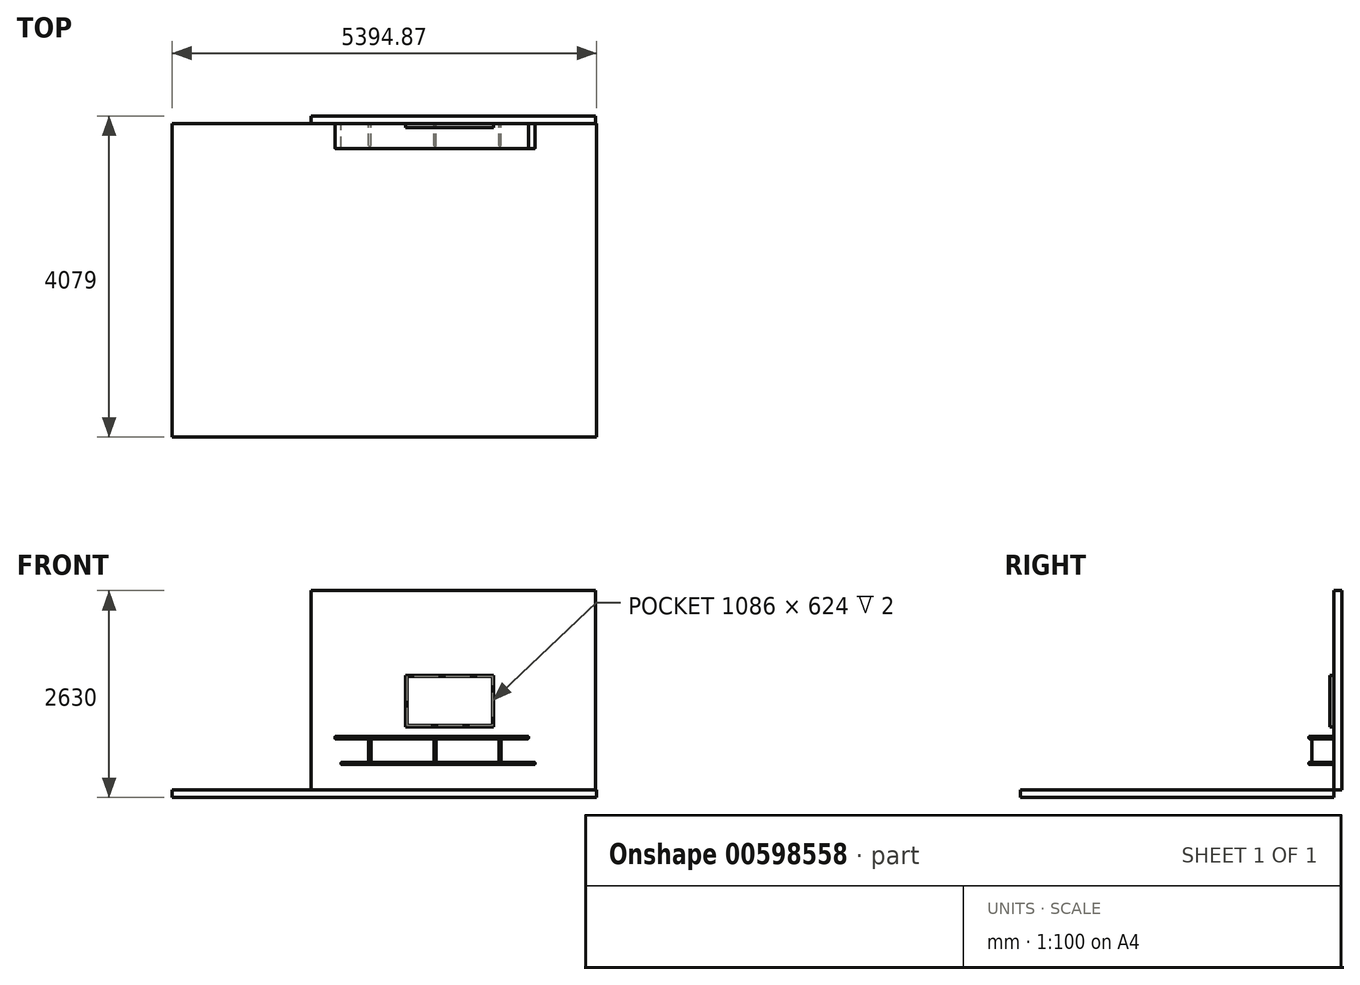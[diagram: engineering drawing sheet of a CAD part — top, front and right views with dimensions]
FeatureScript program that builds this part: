
annotation { "Feature Type Name" : "Feature", "Feature Type Description" : "" }
export const myFeature = defineFeature(function(context is Context, id is Id, definition is map)
    precondition{}
    {
        {
            var Q0;
            Q0=qCreatedBy(makeId("Front.planeOp"),FACE);
            var sketch = newSketch(context, id + "F0", { "sketchPlane" : qUnion([Q0])});
            skLineSegment(sketch, "E0.bottom", {"start": v(-1805, 0) * mm, "end": v(1805, 0) * mm});
            skLineSegment(sketch, "E0.top", {"start": v(-1805, 2530) * mm, "end": v(1805, 2530) * mm});
            skLineSegment(sketch, "E0.left", {"start": v(-1805, 0) * mm, "end": v(-1805, 2530) * mm});
            skLineSegment(sketch, "E0.right", {"start": v(1805, 0) * mm, "end": v(1805, 2530) * mm});
            skPoint(sketch, "E1", {"position": v(0, 0) * mm});
            skSolve(sketch);
        }
        {
            var Q0;
            Q0=makeQuery(id+"F0.imprint","IMPRINT",FACE,{"disambiguationData":[TD([[makeQuery(id+"F0.imprint","IMPRINT",EDGE,{"derivedFrom":sQuery(id+"F0.wireOp",EDGE,"E0.bottom")}),1.0]])]});
            extrude(context, id + "F1", {"entities" : qUnion([Q0]), "oppositeDirection" : true, "depth" : 100 * mm, "offsetDistance" : 25 * mm});
        }
        {
            var Q0;
            Q0=qCreatedBy(makeId("Top.planeOp"),FACE);
            var sketch = newSketch(context, id + "F2", { "sketchPlane" : qUnion([Q0])});
            skLineSegment(sketch, "E2.bottom", {"start": v(1820.18, 0) * mm, "end": v(-3574.69, 0) * mm});
            skLineSegment(sketch, "E2.top", {"start": v(1820.18, -3979) * mm, "end": v(-3574.69, -3979) * mm});
            skLineSegment(sketch, "E2.left", {"start": v(1820.18, 0) * mm, "end": v(1820.18, -3979) * mm});
            skLineSegment(sketch, "E2.right", {"start": v(-3574.69, 0) * mm, "end": v(-3574.69, -3979) * mm});
            skSolve(sketch);
        }
        {
            var Q0;
            Q0 = qSketchRegion(id + "F2", true);
            extrude(context, id + "F3", {"entities" : qUnion([Q0]), "operationType" : NewBodyOperationType.ADD, "oppositeDirection" : true, "depth" : 100 * mm, "offsetDistance" : 25 * mm});
        }
        {
            var Q0;
            Q0=makeQuery(id+"F1.opExtrude","CAP_FACE",FACE,{"disambiguationData":[OSD([sQuery(id+"F0.wireOp",EDGE,"E0.bottom"),sQuery(id+"F0.wireOp",EDGE,"E0.top"),sQuery(id+"F0.wireOp",EDGE,"E0.left"),sQuery(id+"F0.wireOp",EDGE,"E0.right")])],"isStart":true});
            var sketch = newSketch(context, id + "F4", { "sketchPlane" : qUnion([Q0])});
            skLineSegment(sketch, "E3.bottom", {"start": v(511, 800) * mm, "end": v(-605, 800) * mm});
            skLineSegment(sketch, "E3.top", {"start": v(511, 1454) * mm, "end": v(-605, 1454) * mm});
            skLineSegment(sketch, "E3.left", {"start": v(511, 800) * mm, "end": v(511, 1454) * mm});
            skLineSegment(sketch, "E3.right", {"start": v(-605, 800) * mm, "end": v(-605, 1454) * mm});
            skPoint(sketch, "E3.middle", {"position": v(-47, 1127) * mm});
            skSolve(sketch);
        }
        {
            var Q0;
            Q0 = qSketchRegion(id + "F4", true);
            extrude(context, id + "F5", {"entities" : qUnion([Q0]), "depth" : 50 * mm, "offsetDistance" : 25 * mm});
        }
        {
            var Q0;
            Q0=makeQuery(id+"F5.opExtrude","CAP_FACE",FACE,{"disambiguationData":[OSD([sQuery(id+"F4.wireOp",EDGE,"E3.bottom"),sQuery(id+"F4.wireOp",EDGE,"E3.top"),sQuery(id+"F4.wireOp",EDGE,"E3.left"),sQuery(id+"F4.wireOp",EDGE,"E3.right")])],"isStart":false});
            var sketch = newSketch(context, id + "F6", { "sketchPlane" : qUnion([Q0])});
            skLineSegment(sketch, "E4.bottom", {"start": v(-590, 1439) * mm, "end": v(496, 1439) * mm});
            skLineSegment(sketch, "E4.top", {"start": v(-590, 815) * mm, "end": v(496, 815) * mm});
            skLineSegment(sketch, "E4.left", {"start": v(-590, 1439) * mm, "end": v(-590, 815) * mm});
            skLineSegment(sketch, "E4.right", {"start": v(496, 1439) * mm, "end": v(496, 815) * mm});
            skSolve(sketch);
        }
        {
            var Q0;
            Q0 = qSketchRegion(id + "F6", true);
            extrude(context, id + "F7", {"entities" : qUnion([Q0]), "operationType" : NewBodyOperationType.REMOVE, "oppositeDirection" : true, "depth" : 2 * mm, "offsetDistance" : 25 * mm});
        }
        {
            var Q0;
            Q0=makeQuery(id+"F1.opExtrude","CAP_FACE",FACE,{"disambiguationData":[OSD([sQuery(id+"F0.wireOp",EDGE,"E0.bottom"),sQuery(id+"F0.wireOp",EDGE,"E0.top"),sQuery(id+"F0.wireOp",EDGE,"E0.left"),sQuery(id+"F0.wireOp",EDGE,"E0.right")])],"isStart":true});
            var sketch = newSketch(context, id + "F8", { "sketchPlane" : qUnion([Q0])});
            skLineSegment(sketch, "E5.bottom", {"start": v(-1505, 676) * mm, "end": v(955, 676) * mm});
            skLineSegment(sketch, "E5.top", {"start": v(-1505, 648) * mm, "end": v(955, 648) * mm});
            skLineSegment(sketch, "E5.left", {"start": v(-1505, 676) * mm, "end": v(-1505, 648) * mm});
            skLineSegment(sketch, "E5.right", {"start": v(955, 676) * mm, "end": v(955, 648) * mm});
            skLineSegment(sketch, "E6.bottom", {"start": v(-1424.33, 348) * mm, "end": v(1035.67, 348) * mm});
            skLineSegment(sketch, "E6.top", {"start": v(-1424.33, 320) * mm, "end": v(1035.67, 320) * mm});
            skLineSegment(sketch, "E6.left", {"start": v(-1424.33, 348) * mm, "end": v(-1424.33, 320) * mm});
            skLineSegment(sketch, "E6.right", {"start": v(1035.67, 348) * mm, "end": v(1035.67, 320) * mm});
            skSolve(sketch);
        }
        {
            var Q0;
            Q0 = qSketchRegion(id + "F8", true);
            extrude(context, id + "F9", {"entities" : qUnion([Q0]), "depth" : 315 * mm, "offsetDistance" : 25 * mm});
        }
        {
            var Q0;
            Q0=makeQuery(id+"F1.opExtrude","CAP_FACE",FACE,{"disambiguationData":[OSD([sQuery(id+"F0.wireOp",EDGE,"E0.bottom"),sQuery(id+"F0.wireOp",EDGE,"E0.top"),sQuery(id+"F0.wireOp",EDGE,"E0.left"),sQuery(id+"F0.wireOp",EDGE,"E0.right")])],"isStart":true});
            var sketch = newSketch(context, id + "F10", { "sketchPlane" : qUnion([Q0])});
            skLineSegment(sketch, "E7.bottom", {"start": v(-1074.33, 348) * mm, "end": v(-1046.33, 348) * mm});
            skLineSegment(sketch, "E7.top", {"start": v(-1074.33, 648) * mm, "end": v(-1046.33, 648) * mm});
            skLineSegment(sketch, "E7.left", {"start": v(-1074.33, 348) * mm, "end": v(-1074.33, 648) * mm});
            skLineSegment(sketch, "E7.right", {"start": v(-1046.33, 348) * mm, "end": v(-1046.33, 648) * mm});
            skLineSegment(sketch, "E8.bottom", {"start": v(577, 348) * mm, "end": v(605, 348) * mm});
            skLineSegment(sketch, "E8.top", {"start": v(577, 648) * mm, "end": v(605, 648) * mm});
            skLineSegment(sketch, "E8.left", {"start": v(577, 348) * mm, "end": v(577, 648) * mm});
            skLineSegment(sketch, "E8.right", {"start": v(605, 348) * mm, "end": v(605, 648) * mm});
            skLineSegment(sketch, "E9.bottom", {"start": v(-247.43, 348) * mm, "end": v(-219.43, 348) * mm});
            skLineSegment(sketch, "E9.top", {"start": v(-247.43, 648) * mm, "end": v(-219.43, 648) * mm});
            skLineSegment(sketch, "E9.left", {"start": v(-247.43, 348) * mm, "end": v(-247.43, 648) * mm});
            skLineSegment(sketch, "E9.right", {"start": v(-219.43, 348) * mm, "end": v(-219.43, 648) * mm});
            skSolve(sketch);
        }
        {
            var Q0;
            Q0 = qSketchRegion(id + "F10", true);
            extrude(context, id + "F11", {"entities" : qUnion([Q0]), "depth" : 280 * mm, "offsetDistance" : 25 * mm});
        }
        {
            var Q0;
            Q0=makeQuery(id+"F9.opExtrude","CAP_EDGE",EDGE,{"disambiguationData":[OSD([sQuery(id+"F8.wireOp",EDGE,"E5.left")])],"isStart":false});
            var Q1;
            Q1=makeQuery(id+"F9.opExtrude","SWEPT_EDGE",EDGE,{"disambiguationData":[OSD([sQuery(id+"F8.wireOp",EDGE,"E5.bottom"),sQuery(id+"F8.wireOp",EDGE,"E5.left")])]});
            var Q2;
            Q2=makeQuery(id+"F9.opExtrude","SWEPT_EDGE",EDGE,{"disambiguationData":[OSD([sQuery(id+"F8.wireOp",EDGE,"E5.top"),sQuery(id+"F8.wireOp",EDGE,"E5.left")])]});
            var Q3;
            Q3=makeQuery(id+"F9.opExtrude","CAP_EDGE",EDGE,{"disambiguationData":[OSD([sQuery(id+"F8.wireOp",EDGE,"E5.top")])],"isStart":false});
            var Q4;
            Q4=makeQuery(id+"F9.opExtrude","CAP_EDGE",EDGE,{"disambiguationData":[OSD([sQuery(id+"F8.wireOp",EDGE,"E5.bottom")])],"isStart":false});
            var Q5;
            Q5=makeQuery(id+"F9.opExtrude","SWEPT_EDGE",EDGE,{"disambiguationData":[OSD([sQuery(id+"F8.wireOp",EDGE,"E6.bottom"),sQuery(id+"F8.wireOp",EDGE,"E6.left")])]});
            var Q6;
            Q6=makeQuery(id+"F9.opExtrude","SWEPT_EDGE",EDGE,{"disambiguationData":[OSD([sQuery(id+"F8.wireOp",EDGE,"E6.top"),sQuery(id+"F8.wireOp",EDGE,"E6.left")])]});
            var Q7;
            Q7=makeQuery(id+"F9.opExtrude","CAP_EDGE",EDGE,{"disambiguationData":[OSD([sQuery(id+"F8.wireOp",EDGE,"E6.left")])],"isStart":false});
            var Q8;
            Q8=makeQuery(id+"F9.opExtrude","CAP_EDGE",EDGE,{"disambiguationData":[OSD([sQuery(id+"F8.wireOp",EDGE,"E6.top")])],"isStart":false});
            var Q9;
            Q9=makeQuery(id+"F9.opExtrude","SWEPT_EDGE",EDGE,{"disambiguationData":[OSD([sQuery(id+"F8.wireOp",EDGE,"E5.bottom"),sQuery(id+"F8.wireOp",EDGE,"E5.right")])]});
            var Q10;
            Q10=makeQuery(id+"F9.opExtrude","CAP_EDGE",EDGE,{"disambiguationData":[OSD([sQuery(id+"F8.wireOp",EDGE,"E6.right")])],"isStart":false});
            var Q11;
            Q11=makeQuery(id+"F9.opExtrude","SWEPT_EDGE",EDGE,{"disambiguationData":[OSD([sQuery(id+"F8.wireOp",EDGE,"E6.top"),sQuery(id+"F8.wireOp",EDGE,"E6.right")])]});
            var Q12;
            Q12=makeQuery(id+"F9.opExtrude","SWEPT_EDGE",EDGE,{"disambiguationData":[OSD([sQuery(id+"F8.wireOp",EDGE,"E6.bottom"),sQuery(id+"F8.wireOp",EDGE,"E6.right")])]});
            var Q13;
            Q13=makeQuery(id+"F9.opExtrude","SWEPT_EDGE",EDGE,{"disambiguationData":[OSD([sQuery(id+"F8.wireOp",EDGE,"E5.top"),sQuery(id+"F8.wireOp",EDGE,"E5.right")])]});
            var Q14;
            Q14=makeQuery(id+"F9.opExtrude","CAP_EDGE",EDGE,{"disambiguationData":[OSD([sQuery(id+"F8.wireOp",EDGE,"E5.right")])],"isStart":false});
            var Q15;
            Q15=makeQuery(id+"F9.opExtrude","CAP_EDGE",EDGE,{"disambiguationData":[OSD([sQuery(id+"F8.wireOp",EDGE,"E6.bottom")])],"isStart":false});
            fillet(context, id + "F12", {"entities" : qUnion([Q0, Q1, Q2, Q3, Q4, Q5, Q6, Q7, Q8, Q9, Q10, Q11, Q12, Q13, Q14, Q15]), "radius" : 5 * mm, "tangentPropagation" : true, "allowEdgeOverflow" : false});
        }
        {
            var Q0;
            Q0=makeQuery(id+"F11.opExtrude","CAP_EDGE",EDGE,{"disambiguationData":[OSD([sQuery(id+"F10.wireOp",EDGE,"E7.left")])],"isStart":false});
            var Q1;
            Q1=makeQuery(id+"F11.opExtrude","CAP_EDGE",EDGE,{"disambiguationData":[OSD([sQuery(id+"F10.wireOp",EDGE,"E9.left")])],"isStart":false});
            var Q2;
            Q2=makeQuery(id+"F11.opExtrude","CAP_EDGE",EDGE,{"disambiguationData":[OSD([sQuery(id+"F10.wireOp",EDGE,"E8.left")])],"isStart":false});
            var Q3;
            Q3=makeQuery(id+"F11.opExtrude","CAP_EDGE",EDGE,{"disambiguationData":[OSD([sQuery(id+"F10.wireOp",EDGE,"E7.right")])],"isStart":false});
            var Q4;
            Q4=makeQuery(id+"F11.opExtrude","CAP_EDGE",EDGE,{"disambiguationData":[OSD([sQuery(id+"F10.wireOp",EDGE,"E9.right")])],"isStart":false});
            var Q5;
            Q5=makeQuery(id+"F11.opExtrude","CAP_EDGE",EDGE,{"disambiguationData":[OSD([sQuery(id+"F10.wireOp",EDGE,"E8.right")])],"isStart":false});
            fillet(context, id + "F13", {"entities" : qUnion([Q0, Q1, Q2, Q3, Q4, Q5]), "radius" : 5 * mm, "tangentPropagation" : true, "allowEdgeOverflow" : false});
        }
    });
